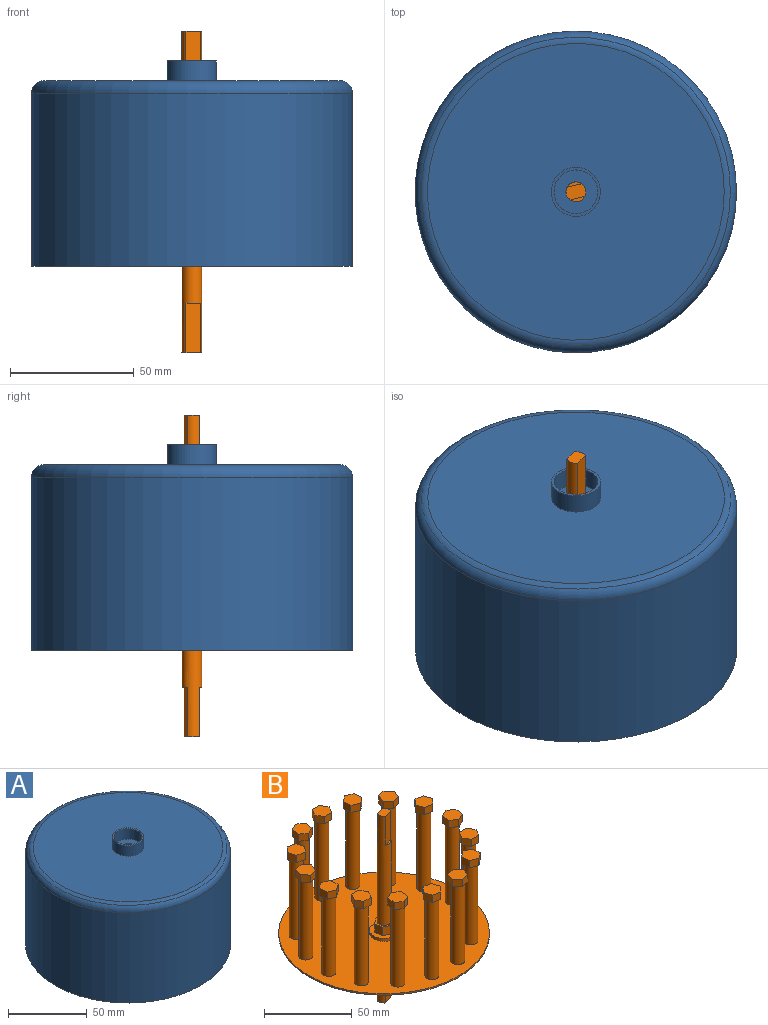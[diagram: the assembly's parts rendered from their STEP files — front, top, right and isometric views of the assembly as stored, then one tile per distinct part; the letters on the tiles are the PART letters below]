
ASSEMBLY  parts=2 mates=1
PART A: 41 faces, bbox 140.7x140.7x83 mm
  f0: plane 17.7x17.7mm, normal (0,0,1), area 195.7mm2, adj f1,f38
  f1: cylinder r=4mm len=8mm, axis (0,0,1), area 25.1mm2, adj f0,f2
  f2: plane 125x125mm, normal (0,0,-1), area 10500.5mm2, adj f1,f4,f6,f8,f10,f12,f14,f16
  f3: plane 120x120mm, normal (0,0,1), area 10998.4mm2, adj f37,f39
  f4: cylinder r=6.04mm len=12.09mm, axis (0,0,1), area 121.5mm2, adj f2,f5
  f5: plane 12.09x12.09mm, normal (0,0,-1), area 114.7mm2, adj f4
  f6: cylinder r=6.04mm len=12.09mm, axis (0,0,1), area 121.5mm2, adj f2,f7
  f7: plane 12.09x12.09mm, normal (0,0,-1), area 114.7mm2, adj f6
  f8: cylinder r=6.04mm len=12.09mm, axis (0,0,1), area 121.5mm2, adj f2,f9
  f9: plane 12.09x12.09mm, normal (0,0,-1), area 114.7mm2, adj f8
  f10: cylinder r=6.04mm len=12.09mm, axis (0,0,1), area 121.5mm2, adj f2,f11
  f11: plane 12.09x12.09mm, normal (0,0,-1), area 114.7mm2, adj f10
  f12: cylinder r=6.04mm len=12.09mm, axis (0,0,1), area 121.5mm2, adj f2,f13
  f13: plane 12.09x12.09mm, normal (0,0,-1), area 114.7mm2, adj f12
  f14: cylinder r=6.04mm len=12.09mm, axis (0,0,1), area 121.5mm2, adj f2,f15
  f15: plane 12.09x12.09mm, normal (0,0,-1), area 114.7mm2, adj f14
  f16: cylinder r=6.04mm len=12.09mm, axis (0,0,1), area 121.5mm2, adj f2,f17
  f17: plane 12.09x12.09mm, normal (0,0,-1), area 114.7mm2, adj f16
  f18: cylinder r=6.04mm len=12.09mm, axis (0,0,1), area 121.5mm2, adj f2,f19
  f19: plane 12.09x12.09mm, normal (0,0,-1), area 114.7mm2, adj f18
  f20: cylinder r=6.04mm len=12.09mm, axis (0,0,1), area 121.5mm2, adj f2,f21
  f21: plane 12.09x12.09mm, normal (0,0,-1), area 114.7mm2, adj f20
  f22: cylinder r=6.04mm len=12.09mm, axis (0,0,1), area 121.5mm2, adj f2,f23
  f23: plane 12.09x12.09mm, normal (0,0,-1), area 114.7mm2, adj f22
  f24: cylinder r=6.04mm len=12.09mm, axis (0,0,1), area 121.5mm2, adj f2,f25
  f25: plane 12.09x12.09mm, normal (0,0,-1), area 114.7mm2, adj f24
  f26: cylinder r=6.04mm len=12.09mm, axis (0,0,1), area 121.5mm2, adj f2,f27
  f27: plane 12.09x12.09mm, normal (0,0,-1), area 114.7mm2, adj f26
  f28: cylinder r=6.04mm len=12.09mm, axis (0,0,1), area 121.5mm2, adj f2,f29
  f29: plane 12.09x12.09mm, normal (0,0,-1), area 114.7mm2, adj f28
  f30: cylinder r=6.04mm len=12.09mm, axis (0,0,1), area 121.5mm2, adj f2,f31
  f31: plane 12.09x12.09mm, normal (0,0,-1), area 114.7mm2, adj f30
  f32: cylinder r=6.04mm len=12.09mm, axis (0,0,1), area 121.5mm2, adj f2,f33
  f33: plane 12.09x12.09mm, normal (0,0,-1), area 114.7mm2, adj f32
  f34: cylinder r=62.5mm len=125mm, axis (0,0,1), area 29059.7mm2, adj f2,f36
  f35: cylinder r=65mm len=130mm, axis (0,0,1), area 28588.5mm2, adj f36,f37
  f36: plane 130x130mm, normal (0,0,-1), area 1001.4mm2, adj f34,f35
  f37: torus R=60mm, axis (0,0,1), area 3118mm2, adj f3,f35
  f38: cylinder r=8.85mm len=17.7mm, axis (0,0,-1), area 444.7mm2, adj f0,f40
  f39: cylinder r=9.96mm len=19.91mm, axis (0,0,-1), area 500.4mm2, adj f3,f40
  f40: plane 19.91x19.91mm, normal (0,0,1), area 65.4mm2, adj f38,f39
PART B: 168 faces, bbox 120x120x130 mm
  f0: plane 5.89x2.11mm, normal (0,0,-1), area 5.8mm2, adj f161,f166
  f1: plane 5.89x2.11mm, normal (0,0,-1), area 5.8mm2, adj f161,f165
  f2: plane 5.89x2.11mm, normal (0,0,1), area 5.8mm2, adj f144,f163
  f3: plane 5.89x2.11mm, normal (0,0,1), area 5.8mm2, adj f144,f162
  f4: plane 120x120mm, normal (0,0,1), area 10338.3mm2, adj f5,f7,f8,f9,f10,f11,f12,f13
  f5: cylinder r=60mm len=120mm, axis (0,0,-1), area 377mm2, adj f4,f6
  f6: plane 120x120mm, normal (0,0,-1), area 11092.3mm2, adj f5,f152
  f7: cylinder r=4mm len=55mm, axis (0,0,-1), area 1382.3mm2, adj f4,f29
  f8: cylinder r=4mm len=55mm, axis (0,0,-1), area 1382.3mm2, adj f4,f37
  f9: cylinder r=4mm len=55mm, axis (0,0,-1), area 1382.3mm2, adj f4,f45
  f10: cylinder r=4mm len=55mm, axis (0,0,-1), area 1382.3mm2, adj f4,f53
  f11: cylinder r=4mm len=55mm, axis (0,0,-1), area 1382.3mm2, adj f4,f61
  f12: cylinder r=4mm len=55mm, axis (0,0,-1), area 1382.3mm2, adj f4,f69
  f13: cylinder r=4mm len=55mm, axis (0,0,-1), area 1382.3mm2, adj f4,f77
  f14: cylinder r=4mm len=55mm, axis (0,0,-1), area 1382.3mm2, adj f4,f85
  f15: cylinder r=4mm len=55mm, axis (0,0,-1), area 1382.3mm2, adj f4,f93
  f16: cylinder r=4mm len=55mm, axis (0,0,-1), area 1382.3mm2, adj f4,f101
  f17: cylinder r=4mm len=55mm, axis (0,0,-1), area 1382.3mm2, adj f4,f109
  f18: cylinder r=4mm len=55mm, axis (0,0,-1), area 1382.3mm2, adj f4,f117
  f19: cylinder r=4mm len=55mm, axis (0,0,-1), area 1382.3mm2, adj f4,f125
  f20: cylinder r=4mm len=55mm, axis (0,0,-1), area 1382.3mm2, adj f4,f133
  f21: cylinder r=4mm len=55mm, axis (0,0,-1), area 1382.3mm2, adj f4,f141
  f22: plane 5x4.98mm, normal (-0.87,-0.5,0), area 28.8mm2, adj f23,f27,f28,f29
  f23: plane 5.75x5mm, normal (0,-1,0), area 28.8mm2, adj f22,f24,f28,f29
  f24: plane 5x4.98mm, normal (0.87,-0.5,0), area 28.8mm2, adj f23,f25,f28,f29
  f25: plane 5x4.98mm, normal (0.87,0.5,0), area 28.8mm2, adj f24,f26,f28,f29
  f26: plane 5.75x5mm, normal (0,1,0), area 28.8mm2, adj f25,f27,f28,f29
  f27: plane 5x4.98mm, normal (-0.87,0.5,0), area 28.8mm2, adj f22,f26,f28,f29
  f28: plane 11.5x9.96mm, normal (0,0,1), area 86mm2, adj f22,f23,f24,f25,f26,f27
  f29: plane 11.5x9.96mm, normal (0,0,-1), area 35.7mm2, adj f7,f22,f23,f24,f25,f26,f27
  f30: plane 5.26x5mm, normal (-0.41,0.91,0), area 28.8mm2, adj f31,f35,f36,f37
  f31: plane 5.72x5mm, normal (-0.99,0.1,0), area 28.8mm2, adj f30,f32,f36,f37
  f32: plane 5x4.65mm, normal (-0.59,-0.81,0), area 28.8mm2, adj f31,f33,f36,f37
  f33: plane 5.26x5mm, normal (0.41,-0.91,0), area 28.8mm2, adj f32,f34,f36,f37
  f34: plane 5.72x5mm, normal (0.99,-0.1,0), area 28.8mm2, adj f33,f35,f36,f37
  f35: plane 5x4.65mm, normal (0.59,0.81,0), area 28.8mm2, adj f30,f34,f36,f37
  f36: plane 11.44x10.51mm, normal (0,0,1), area 86mm2, adj f30,f31,f32,f33,f34,f35
  f37: plane 11.44x10.51mm, normal (0,0,-1), area 35.7mm2, adj f8,f30,f31,f32,f33,f34,f35
  f38: plane 5x4.27mm, normal (-0.74,0.67,0), area 28.8mm2, adj f39,f43,f44,f45
  f39: plane 5.47x5mm, normal (-0.95,-0.31,0), area 28.8mm2, adj f38,f40,f44,f45
  f40: plane 5.63x5mm, normal (-0.21,-0.98,0), area 28.8mm2, adj f39,f41,f44,f45
  f41: plane 5x4.27mm, normal (0.74,-0.67,0), area 28.8mm2, adj f40,f42,f44,f45
  f42: plane 5.47x5mm, normal (0.95,0.31,0), area 28.8mm2, adj f41,f43,f44,f45
  f43: plane 5.63x5mm, normal (0.21,0.98,0), area 28.8mm2, adj f38,f42,f44,f45
  f44: plane 11.25x10.94mm, normal (0,0,1), area 86mm2, adj f38,f39,f40,f41,f42,f43
  f45: plane 11.25x10.94mm, normal (0,0,-1), area 35.7mm2, adj f9,f38,f39,f40,f41,f42,f43
  f46: plane 5.47x5mm, normal (-0.95,0.31,0), area 28.8mm2, adj f47,f51,f52,f53
  f47: plane 5x4.27mm, normal (-0.74,-0.67,0), area 28.8mm2, adj f46,f48,f52,f53
  f48: plane 5.63x5mm, normal (0.21,-0.98,0), area 28.8mm2, adj f47,f49,f52,f53
  f49: plane 5.47x5mm, normal (0.95,-0.31,0), area 28.8mm2, adj f48,f50,f52,f53
  f50: plane 5x4.27mm, normal (0.74,0.67,0), area 28.8mm2, adj f49,f51,f52,f53
  f51: plane 5.63x5mm, normal (-0.21,0.98,0), area 28.8mm2, adj f46,f50,f52,f53
  f52: plane 11.25x10.94mm, normal (0,0,1), area 86mm2, adj f46,f47,f48,f49,f50,f51
  f53: plane 11.25x10.94mm, normal (0,0,-1), area 35.7mm2, adj f10,f46,f47,f48,f49,f50,f51
  f54: plane 5.72x5mm, normal (-0.99,-0.1,0), area 28.8mm2, adj f55,f59,f60,f61
  f55: plane 5.26x5mm, normal (-0.41,-0.91,0), area 28.8mm2, adj f54,f56,f60,f61
  f56: plane 5x4.65mm, normal (0.59,-0.81,0), area 28.8mm2, adj f55,f57,f60,f61
  f57: plane 5.72x5mm, normal (0.99,0.1,0), area 28.8mm2, adj f56,f58,f60,f61
  f58: plane 5.26x5mm, normal (0.41,0.91,0), area 28.8mm2, adj f57,f59,f60,f61
  f59: plane 5x4.65mm, normal (-0.59,0.81,0), area 28.8mm2, adj f54,f58,f60,f61
  f60: plane 11.44x10.51mm, normal (0,0,1), area 86mm2, adj f54,f55,f56,f57,f58,f59
  f61: plane 11.44x10.51mm, normal (0,0,-1), area 35.7mm2, adj f11,f54,f55,f56,f57,f58,f59
  f62: plane 5x4.98mm, normal (-0.87,-0.5,0), area 28.8mm2, adj f63,f67,f68,f69
  f63: plane 5.75x5mm, normal (0,-1,0), area 28.8mm2, adj f62,f64,f68,f69
  f64: plane 5x4.98mm, normal (0.87,-0.5,0), area 28.8mm2, adj f63,f65,f68,f69
  f65: plane 5x4.98mm, normal (0.87,0.5,0), area 28.8mm2, adj f64,f66,f68,f69
  f66: plane 5.75x5mm, normal (0,1,0), area 28.8mm2, adj f65,f67,f68,f69
  f67: plane 5x4.98mm, normal (-0.87,0.5,0), area 28.8mm2, adj f62,f66,f68,f69
  f68: plane 11.5x9.96mm, normal (0,0,1), area 86mm2, adj f62,f63,f64,f65,f66,f67
  f69: plane 11.5x9.96mm, normal (0,0,-1), area 35.7mm2, adj f12,f62,f63,f64,f65,f66,f67
  f70: plane 5x4.65mm, normal (-0.59,-0.81,0), area 28.8mm2, adj f71,f75,f76,f77
  f71: plane 5.26x5mm, normal (0.41,-0.91,0), area 28.8mm2, adj f70,f72,f76,f77
  f72: plane 5.72x5mm, normal (0.99,-0.1,0), area 28.8mm2, adj f71,f73,f76,f77
  f73: plane 5x4.65mm, normal (0.59,0.81,0), area 28.8mm2, adj f72,f74,f76,f77
  f74: plane 5.26x5mm, normal (-0.41,0.91,0), area 28.8mm2, adj f73,f75,f76,f77
  f75: plane 5.72x5mm, normal (-0.99,0.1,0), area 28.8mm2, adj f70,f74,f76,f77
  f76: plane 11.44x10.51mm, normal (0,0,1), area 86mm2, adj f70,f71,f72,f73,f74,f75
  f77: plane 11.44x10.51mm, normal (0,0,-1), area 35.7mm2, adj f13,f70,f71,f72,f73,f74,f75
  f78: plane 5.63x5mm, normal (-0.21,-0.98,0), area 28.8mm2, adj f79,f83,f84,f85
  f79: plane 5x4.27mm, normal (0.74,-0.67,0), area 28.8mm2, adj f78,f80,f84,f85
  f80: plane 5.47x5mm, normal (0.95,0.31,0), area 28.8mm2, adj f79,f81,f84,f85
  f81: plane 5.63x5mm, normal (0.21,0.98,0), area 28.8mm2, adj f80,f82,f84,f85
  f82: plane 5x4.27mm, normal (-0.74,0.67,0), area 28.8mm2, adj f81,f83,f84,f85
  f83: plane 5.47x5mm, normal (-0.95,-0.31,0), area 28.8mm2, adj f78,f82,f84,f85
  f84: plane 11.25x10.94mm, normal (0,0,1), area 86mm2, adj f78,f79,f80,f81,f82,f83
  f85: plane 11.25x10.94mm, normal (0,0,-1), area 35.7mm2, adj f14,f78,f79,f80,f81,f82,f83
  f86: plane 5.63x5mm, normal (0.21,-0.98,0), area 28.8mm2, adj f87,f91,f92,f93
  f87: plane 5.47x5mm, normal (0.95,-0.31,0), area 28.8mm2, adj f86,f88,f92,f93
  f88: plane 5x4.27mm, normal (0.74,0.67,0), area 28.8mm2, adj f87,f89,f92,f93
  f89: plane 5.63x5mm, normal (-0.21,0.98,0), area 28.8mm2, adj f88,f90,f92,f93
  f90: plane 5.47x5mm, normal (-0.95,0.31,0), area 28.8mm2, adj f89,f91,f92,f93
  f91: plane 5x4.27mm, normal (-0.74,-0.67,0), area 28.8mm2, adj f86,f90,f92,f93
  f92: plane 11.25x10.94mm, normal (0,0,1), area 86mm2, adj f86,f87,f88,f89,f90,f91
  f93: plane 11.25x10.94mm, normal (0,0,-1), area 35.7mm2, adj f15,f86,f87,f88,f89,f90,f91
  f94: plane 5x4.65mm, normal (0.59,-0.81,0), area 28.8mm2, adj f95,f99,f100,f101
  f95: plane 5.72x5mm, normal (0.99,0.1,0), area 28.8mm2, adj f94,f96,f100,f101
  f96: plane 5.26x5mm, normal (0.41,0.91,0), area 28.8mm2, adj f95,f97,f100,f101
  f97: plane 5x4.65mm, normal (-0.59,0.81,0), area 28.8mm2, adj f96,f98,f100,f101
  f98: plane 5.72x5mm, normal (-0.99,-0.1,0), area 28.8mm2, adj f97,f99,f100,f101
  f99: plane 5.26x5mm, normal (-0.41,-0.91,0), area 28.8mm2, adj f94,f98,f100,f101
  f100: plane 11.44x10.51mm, normal (0,0,1), area 86mm2, adj f94,f95,f96,f97,f98,f99
  f101: plane 11.44x10.51mm, normal (0,0,-1), area 35.7mm2, adj f16,f94,f95,f96,f97,f98,f99
  f102: plane 5x4.98mm, normal (0.87,-0.5,0), area 28.8mm2, adj f103,f107,f108,f109
  f103: plane 5x4.98mm, normal (0.87,0.5,0), area 28.8mm2, adj f102,f104,f108,f109
  f104: plane 5.75x5mm, normal (0,1,0), area 28.8mm2, adj f103,f105,f108,f109
  f105: plane 5x4.98mm, normal (-0.87,0.5,0), area 28.8mm2, adj f104,f106,f108,f109
  f106: plane 5x4.98mm, normal (-0.87,-0.5,0), area 28.8mm2, adj f105,f107,f108,f109
  f107: plane 5.75x5mm, normal (0,-1,0), area 28.8mm2, adj f102,f106,f108,f109
  f108: plane 11.5x9.96mm, normal (0,0,1), area 86mm2, adj f102,f103,f104,f105,f106,f107
  f109: plane 11.5x9.96mm, normal (0,0,-1), area 35.7mm2, adj f17,f102,f103,f104,f105,f106,f107
  f110: plane 5.72x5mm, normal (0.99,-0.1,0), area 28.8mm2, adj f111,f115,f116,f117
  f111: plane 5x4.65mm, normal (0.59,0.81,0), area 28.8mm2, adj f110,f112,f116,f117
  f112: plane 5.26x5mm, normal (-0.41,0.91,0), area 28.8mm2, adj f111,f113,f116,f117
  f113: plane 5.72x5mm, normal (-0.99,0.1,0), area 28.8mm2, adj f112,f114,f116,f117
  f114: plane 5x4.65mm, normal (-0.59,-0.81,0), area 28.8mm2, adj f113,f115,f116,f117
  f115: plane 5.26x5mm, normal (0.41,-0.91,0), area 28.8mm2, adj f110,f114,f116,f117
  f116: plane 11.44x10.51mm, normal (0,0,1), area 86mm2, adj f110,f111,f112,f113,f114,f115
  f117: plane 11.44x10.51mm, normal (0,0,-1), area 35.7mm2, adj f18,f110,f111,f112,f113,f114,f115
  f118: plane 5.47x5mm, normal (0.95,0.31,0), area 28.8mm2, adj f119,f123,f124,f125
  f119: plane 5.63x5mm, normal (0.21,0.98,0), area 28.8mm2, adj f118,f120,f124,f125
  f120: plane 5x4.27mm, normal (-0.74,0.67,0), area 28.8mm2, adj f119,f121,f124,f125
  f121: plane 5.47x5mm, normal (-0.95,-0.31,0), area 28.8mm2, adj f120,f122,f124,f125
  f122: plane 5.63x5mm, normal (-0.21,-0.98,0), area 28.8mm2, adj f121,f123,f124,f125
  f123: plane 5x4.27mm, normal (0.74,-0.67,0), area 28.8mm2, adj f118,f122,f124,f125
  f124: plane 11.25x10.94mm, normal (0,0,1), area 86mm2, adj f118,f119,f120,f121,f122,f123
  f125: plane 11.25x10.94mm, normal (0,0,-1), area 35.7mm2, adj f19,f118,f119,f120,f121,f122,f123
  f126: plane 5x4.27mm, normal (0.74,0.67,0), area 28.8mm2, adj f127,f131,f132,f133
  f127: plane 5.63x5mm, normal (-0.21,0.98,0), area 28.8mm2, adj f126,f128,f132,f133
  f128: plane 5.47x5mm, normal (-0.95,0.31,0), area 28.8mm2, adj f127,f129,f132,f133
  f129: plane 5x4.27mm, normal (-0.74,-0.67,0), area 28.8mm2, adj f128,f130,f132,f133
  f130: plane 5.63x5mm, normal (0.21,-0.98,0), area 28.8mm2, adj f129,f131,f132,f133
  f131: plane 5.47x5mm, normal (0.95,-0.31,0), area 28.8mm2, adj f126,f130,f132,f133
  f132: plane 11.25x10.94mm, normal (0,0,1), area 86mm2, adj f126,f127,f128,f129,f130,f131
  f133: plane 11.25x10.94mm, normal (0,0,-1), area 35.7mm2, adj f20,f126,f127,f128,f129,f130,f131
  f134: plane 5.26x5mm, normal (0.41,0.91,0), area 28.8mm2, adj f135,f139,f140,f141
  f135: plane 5x4.65mm, normal (-0.59,0.81,0), area 28.8mm2, adj f134,f136,f140,f141
  f136: plane 5.72x5mm, normal (-0.99,-0.1,0), area 28.8mm2, adj f135,f137,f140,f141
  f137: plane 5.26x5mm, normal (-0.41,-0.91,0), area 28.8mm2, adj f136,f138,f140,f141
  f138: plane 5x4.65mm, normal (0.59,-0.81,0), area 28.8mm2, adj f137,f139,f140,f141
  f139: plane 5.72x5mm, normal (0.99,0.1,0), area 28.8mm2, adj f134,f138,f140,f141
  f140: plane 11.44x10.51mm, normal (0,0,1), area 86mm2, adj f134,f135,f136,f137,f138,f139
  f141: plane 11.44x10.51mm, normal (0,0,-1), area 35.7mm2, adj f21,f134,f135,f136,f137,f138,f139
  f142: cylinder r=8.32mm len=16.64mm, axis (0,0,-1), area 104.5mm2, adj f4,f143
  f143: plane 16.64x16.64mm, normal (0,0,1), area 131.5mm2, adj f142,f146,f147,f148,f149,f150,f151
  f144: cylinder r=4mm len=76mm, axis (0,0,-1), area 1636.1mm2, adj f2,f3,f145,f162,f163,f164
  f145: plane 11.44x10.51mm, normal (0,0,1), area 35.7mm2, adj f144,f146,f147,f148,f149,f150,f151
  f146: plane 6x4.65mm, normal (0.59,-0.81,0), area 34.5mm2, adj f143,f145,f147,f151
  f147: plane 6x5.26mm, normal (-0.41,-0.91,0), area 34.5mm2, adj f143,f145,f146,f148
  f148: plane 6x5.72mm, normal (-0.99,-0.1,0), area 34.5mm2, adj f143,f145,f147,f149
  f149: plane 6x4.65mm, normal (-0.59,0.81,0), area 34.5mm2, adj f143,f145,f148,f150
  f150: plane 6x5.26mm, normal (0.41,0.91,0), area 34.5mm2, adj f143,f145,f149,f151
  f151: plane 6x5.72mm, normal (0.99,0.1,0), area 34.5mm2, adj f143,f145,f146,f150
  f152: cylinder r=8.32mm len=16.64mm, axis (0,0,1), area 104.5mm2, adj f6,f153
  f153: plane 16.64x16.64mm, normal (0,0,-1), area 131.5mm2, adj f152,f154,f155,f156,f157,f158,f159
  f154: plane 5.72x3.8mm, normal (0.99,0.1,0), area 21.9mm2, adj f153,f155,f159,f160
  f155: plane 5.26x3.8mm, normal (0.41,0.91,0), area 21.9mm2, adj f153,f154,f156,f160
  f156: plane 4.65x3.8mm, normal (-0.59,0.81,0), area 21.9mm2, adj f153,f155,f157,f160
  f157: plane 5.72x3.8mm, normal (-0.99,-0.1,0), area 21.9mm2, adj f153,f156,f158,f160
  f158: plane 5.26x3.8mm, normal (-0.41,-0.91,0), area 21.9mm2, adj f153,f157,f159,f160
  f159: plane 4.65x3.8mm, normal (0.59,-0.81,0), area 21.9mm2, adj f153,f154,f158,f160
  f160: plane 11.44x10.51mm, normal (0,0,-1), area 35.7mm2, adj f154,f155,f156,f157,f158,f159,f161
  f161: cylinder r=4mm len=39.2mm, axis (0,0,1), area 711.2mm2, adj f0,f1,f160,f165,f166,f167
  f162: plane 20x5.89mm, normal (0.22,-0.98,0), area 120.9mm2, adj f3,f144,f164
  f163: plane 20x5.89mm, normal (-0.22,0.98,0), area 120.9mm2, adj f2,f144,f164
  f164: plane 8x6.45mm, normal (0,0,1), area 38.7mm2, adj f144,f162,f163
  f165: plane 20x5.89mm, normal (0.22,-0.98,0), area 120.9mm2, adj f1,f161,f167
  f166: plane 20x5.89mm, normal (-0.22,0.98,0), area 120.9mm2, adj f0,f161,f167
  f167: plane 8x6.45mm, normal (0,0,-1), area 38.7mm2, adj f161,f165,f166
PLACE A t=(63.07,53.7,88.27)mm
PLACE B t=(63.07,53.7,23.27)mm
MATE revolute A.f35 <-> B.f144  axis (0,0,1) through (63.07,53.7,88.27)mm
